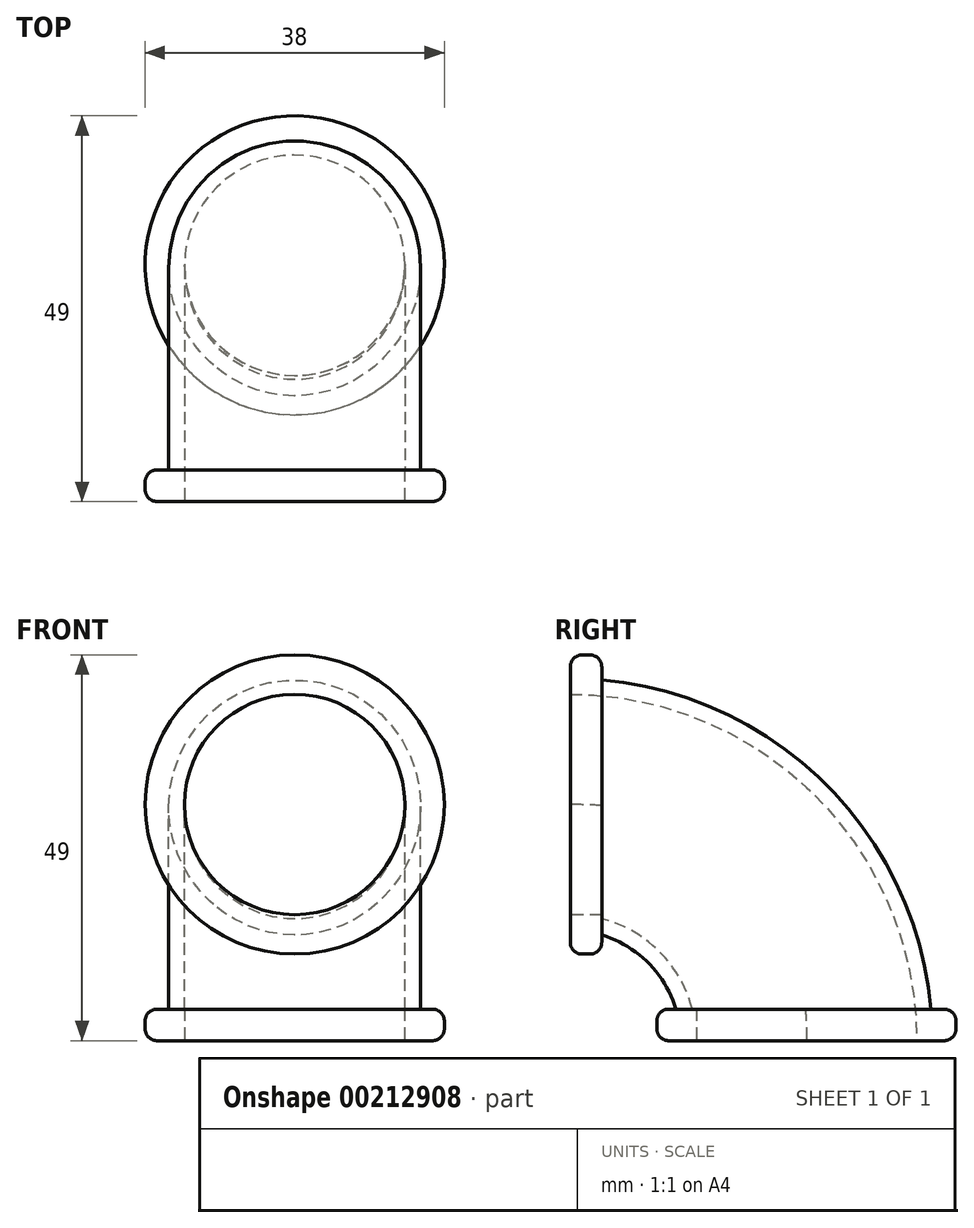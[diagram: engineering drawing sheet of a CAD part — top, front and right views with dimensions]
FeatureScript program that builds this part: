
annotation { "Feature Type Name" : "Feature", "Feature Type Description" : "" }
export const myFeature = defineFeature(function(context is Context, id is Id, definition is map)
    precondition{}
    {
        {
            var Q0;
            Q0=qCreatedBy(makeId("Right.planeOp"),FACE);
            var sketch = newSketch(context, id + "F0", { "sketchPlane" : qUnion([Q0])});
            skArc(sketch, "E0", {"start": v(0, 30) * mm, "mid": v(21.21, 21.21) * mm, "end": v(30, 0) * mm});
            skSolve(sketch);
        }
        {
            var Q0;
            Q0=qCreatedBy(makeId("Top.planeOp"),FACE);
            var sketch = newSketch(context, id + "F1", { "sketchPlane" : qUnion([Q0])});
            skPoint(sketch, "E1.0", {"position": v(0, 30) * mm});
            skCircle(sketch, "E2", {"center": v(0, 30) * mm, "radius": 16 * mm});
            skCircle(sketch, "E3.0", {"center": v(0, 30) * mm, "radius": 14 * mm});
            skSolve(sketch);
        }
        {
            var Q0;
            Q0=makeQuery(id+"F1.imprint","IMPRINT",FACE,{"disambiguationData":[TD([[makeQuery(id+"F1.imprint","IMPRINT",EDGE,{"derivedFrom":sQuery(id+"F1.wireOp",EDGE,"E2")}),1.0]])]});
            var Q1;
            Q1=sQuery(id+"F0.wireOp",EDGE,"E0");
            sweep(context, id + "F2", {"profiles" : qUnion([Q0]), "path" : qUnion([Q1])});
        }
        {
            var Q0;
            Q0=qCreatedBy(makeId("Front.planeOp"),FACE);
            var sketch = newSketch(context, id + "F3", { "sketchPlane" : qUnion([Q0])});
            skCircle(sketch, "E4", {"center": v(0, 30) * mm, "radius": 19 * mm});
            skCircle(sketch, "E5.0", {"center": v(0, 30) * mm, "radius": 14 * mm});
            skSolve(sketch);
        }
        {
            var Q0;
            Q0 = qSketchRegion(id + "F3", true);
            extrude(context, id + "F4", {"entities" : qUnion([Q0]), "operationType" : NewBodyOperationType.ADD, "oppositeDirection" : true, "depth" : 4 * mm});
        }
        {
            var Q0;
            Q0=qCreatedBy(makeId("Top.planeOp"),FACE);
            var sketch = newSketch(context, id + "F5", { "sketchPlane" : qUnion([Q0])});
            skCircle(sketch, "E6", {"center": v(0, 30) * mm, "radius": 19 * mm});
            skCircle(sketch, "E7.0", {"center": v(0, 30) * mm, "radius": 14 * mm});
            skSolve(sketch);
        }
        {
            var Q0;
            Q0 = qSketchRegion(id + "F5", true);
            extrude(context, id + "F6", {"entities" : qUnion([Q0]), "operationType" : NewBodyOperationType.ADD, "depth" : 4 * mm});
        }
        {
            var Q0;
            Q0=makeQuery(id+"F4.opExtrude","CAP_EDGE",EDGE,{"disambiguationData":[OSD([sQuery(id+"F3.wireOp",EDGE,"E4")])],"isStart":false});
            var Q1;
            Q1=makeQuery(id+"F4.opExtrude","CAP_EDGE",EDGE,{"disambiguationData":[OSD([sQuery(id+"F3.wireOp",EDGE,"E4")])],"isStart":true});
            var Q2;
            Q2=makeQuery(id+"F6.opExtrude","CAP_EDGE",EDGE,{"disambiguationData":[OSD([sQuery(id+"F5.wireOp",EDGE,"E6")])],"isStart":false});
            var Q3;
            Q3=makeQuery(id+"F6.opExtrude","CAP_EDGE",EDGE,{"disambiguationData":[OSD([sQuery(id+"F5.wireOp",EDGE,"E6")])],"isStart":true});
            fillet(context, id + "F7", {"entities" : qUnion([Q0, Q1, Q2, Q3]), "radius" : 1.5 * mm, "tangentPropagation" : true, "allowEdgeOverflow" : false});
        }
    });
